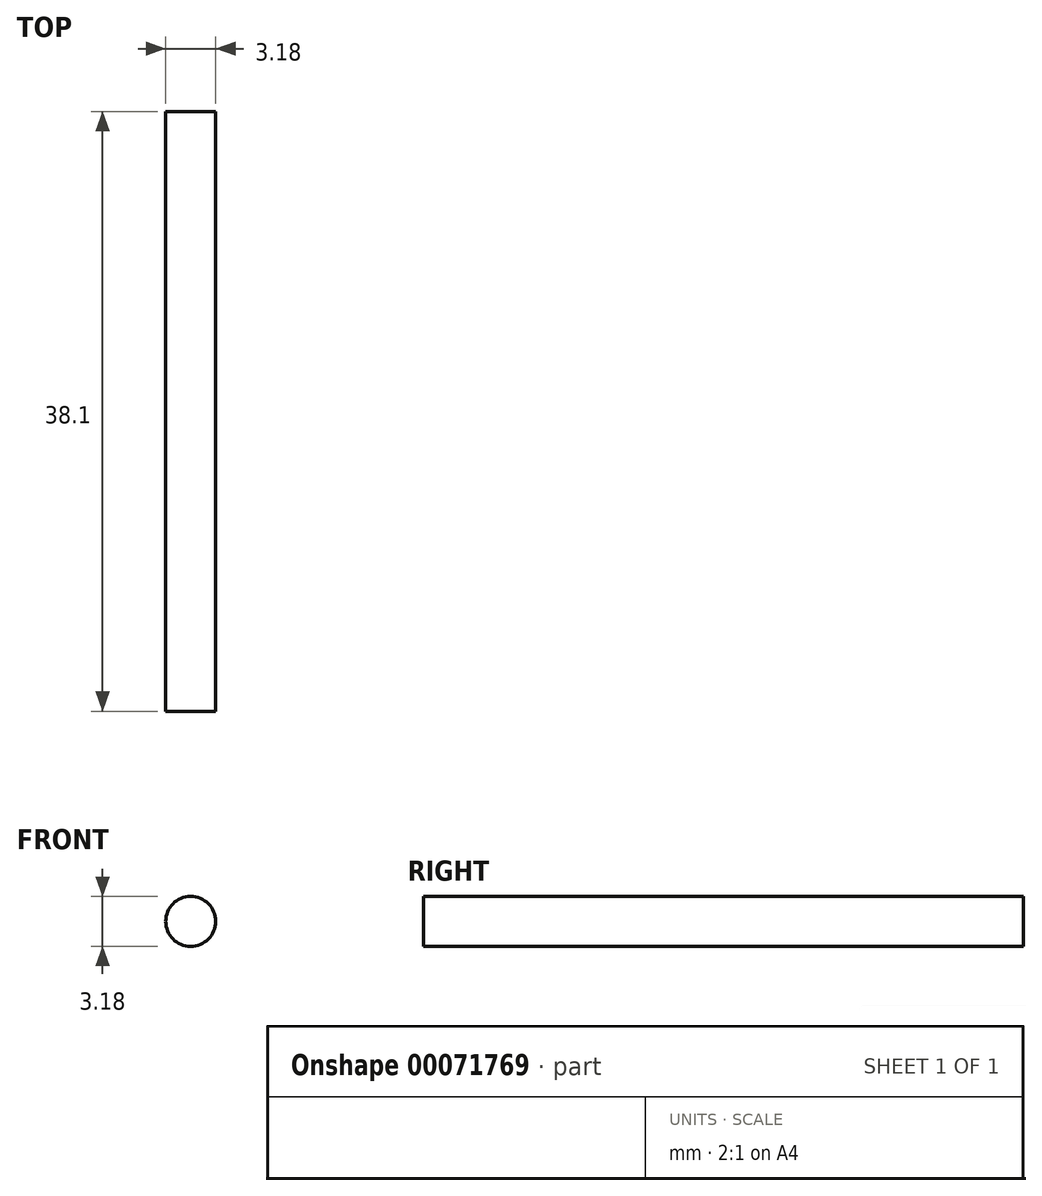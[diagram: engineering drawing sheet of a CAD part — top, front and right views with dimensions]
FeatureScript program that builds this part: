
annotation { "Feature Type Name" : "Feature", "Feature Type Description" : "" }
export const myFeature = defineFeature(function(context is Context, id is Id, definition is map)
    precondition{}
    {
        {
            var Q0;
            Q0=qCreatedBy(makeId("Front.planeOp"),FACE);
            var sketch = newSketch(context, id + "F0", { "sketchPlane" : qUnion([Q0])});
            skCircle(sketch, "E0", {"center": v(0, 0) * mm, "radius": 1.59 * mm});
            skSolve(sketch);
        }
        {
            var Q0;
            Q0=makeQuery(id+"F0.imprint","IMPRINT",FACE,{"disambiguationData":[TD([[makeQuery(id+"F0.imprint","IMPRINT",EDGE,{"derivedFrom":sQuery(id+"F0.wireOp",EDGE,"E0")}),1.0]])]});
            extrude(context, id + "F1", {"entities" : qUnion([Q0]), "depth" : 38.1 * mm});
        }
    });
